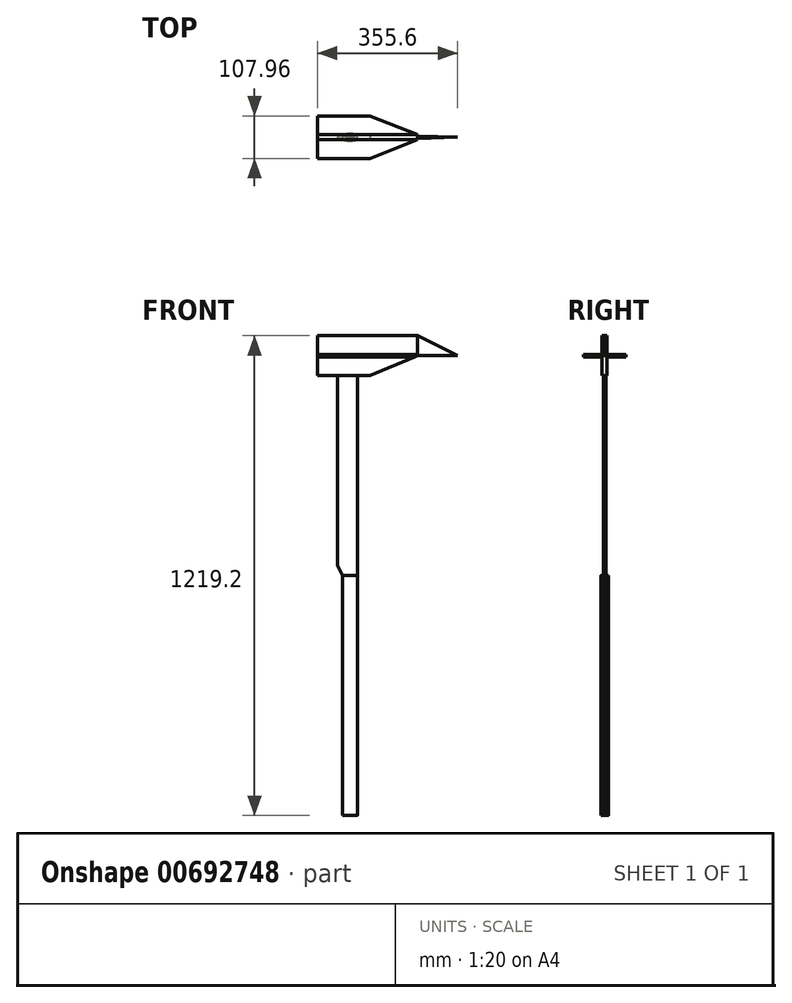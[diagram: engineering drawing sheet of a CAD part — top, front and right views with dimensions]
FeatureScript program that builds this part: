
annotation { "Feature Type Name" : "Feature", "Feature Type Description" : "" }
export const myFeature = defineFeature(function(context is Context, id is Id, definition is map)
    precondition{}
    {
        {
            var Q0;
            Q0=qCreatedBy(makeId("Top.planeOp"),FACE);
            var sketch = newSketch(context, id + "F0", { "sketchPlane" : qUnion([Q0])});
            skLineSegment(sketch, "E0.bottom", {"start": v(25.4, -3.17) * mm, "end": v(-25.4, -3.18) * mm});
            skLineSegment(sketch, "E0.top", {"start": v(25.4, 3.18) * mm, "end": v(-25.4, 3.18) * mm});
            skLineSegment(sketch, "E0.left", {"start": v(25.4, -3.17) * mm, "end": v(25.4, 3.18) * mm});
            skLineSegment(sketch, "E0.right", {"start": v(-25.4, -3.18) * mm, "end": v(-25.4, 3.18) * mm});
            skPoint(sketch, "E0.middle", {"position": v(0, 0) * mm});
            skSolve(sketch);
        }
        {
            var Q0;
            Q0 = qSketchRegion(id + "F0", true);
            extrude(context, id + "F1", {"entities" : qUnion([Q0]), "depth" : 1219.2 * mm, "offsetDistance" : 25.4 * mm});
        }
        {
            var Q0;
            Q0=qCreatedBy(makeId("Top.planeOp"),FACE);
            var sketch = newSketch(context, id + "F2", { "sketchPlane" : qUnion([Q0])});
            skLineSegment(sketch, "E1.bottom", {"start": v(-76.2, 53.98) * mm, "end": v(279.4, 53.98) * mm});
            skLineSegment(sketch, "E1.top", {"start": v(-76.2, -53.98) * mm, "end": v(279.4, -53.98) * mm});
            skLineSegment(sketch, "E1.left", {"start": v(-76.2, 53.98) * mm, "end": v(-76.2, -53.98) * mm});
            skLineSegment(sketch, "E1.right", {"start": v(279.4, 53.98) * mm, "end": v(279.4, -53.98) * mm, "construction": true});
            skPoint(sketch, "E2", {"position": v(279.4, 0) * mm});
            skPoint(sketch, "E3", {"position": v(177.8, 3.18) * mm});
            skPoint(sketch, "E4", {"position": v(177.8, -3.18) * mm});
            skPoint(sketch, "E5", {"position": v(177.8, 6.35) * mm});
            skPoint(sketch, "E6", {"position": v(177.8, -6.35) * mm});
            skPoint(sketch, "E7", {"position": v(57.15, 53.98) * mm});
            skPoint(sketch, "E8", {"position": v(57.16, -53.98) * mm});
            skLineSegment(sketch, "E9", {"start": v(57.15, 53.97) * mm, "end": v(177.8, 6.35) * mm});
            skLineSegment(sketch, "E10", {"start": v(177.8, 6.35) * mm, "end": v(177.8, 3.18) * mm});
            skLineSegment(sketch, "E11", {"start": v(177.8, 3.18) * mm, "end": v(279.4, 0) * mm});
            skLineSegment(sketch, "E12", {"start": v(177.8, -3.18) * mm, "end": v(177.8, -6.35) * mm});
            skLineSegment(sketch, "E13", {"start": v(177.8, -3.18) * mm, "end": v(279.4, 0) * mm});
            skLineSegment(sketch, "E14", {"start": v(177.8, -6.35) * mm, "end": v(57.16, -53.98) * mm});
            skSolve(sketch);
        }
        {
            var Q0;
            Q0 = qSketchRegion(id + "F2", true);
            extrude(context, id + "F3", {"entities" : qUnion([Q0]), "operationType" : NewBodyOperationType.ADD, "depth" : 1219.2 * mm, "offsetDistance" : 25.4 * mm, "hasSecondDirection" : true, "secondDirectionOppositeDirection" : false, "secondDirectionDepth" : 1117.6 * mm});
        }
        {
            var Q0;
            Q0=qCreatedBy(makeId("Front.planeOp"),FACE);
            var sketch = newSketch(context, id + "F4", { "sketchPlane" : qUnion([Q0])});
            skLineSegment(sketch, "E15.bottom", {"start": v(-76.2, 1117.6) * mm, "end": v(177.8, 1117.6) * mm, "construction": true});
            skLineSegment(sketch, "E15.top", {"start": v(-76.2, 1219.2) * mm, "end": v(177.8, 1219.2) * mm, "construction": true});
            skLineSegment(sketch, "E15.left", {"start": v(-76.2, 1117.6) * mm, "end": v(-76.2, 1219.2) * mm, "construction": true});
            skLineSegment(sketch, "E15.right", {"start": v(177.8, 1117.6) * mm, "end": v(177.8, 1219.2) * mm, "construction": true});
            skLineSegment(sketch, "E16.bottom", {"start": v(177.8, 1219.2) * mm, "end": v(279.4, 1219.2) * mm, "construction": true});
            skLineSegment(sketch, "E16.top", {"start": v(177.8, 1168.4) * mm, "end": v(279.4, 1168.4) * mm, "construction": true});
            skLineSegment(sketch, "E16.left", {"start": v(177.8, 1219.2) * mm, "end": v(177.8, 1168.4) * mm, "construction": true});
            skLineSegment(sketch, "E16.right", {"start": v(279.4, 1219.2) * mm, "end": v(279.4, 1168.4) * mm, "construction": true});
            skLineSegment(sketch, "E17", {"start": v(279.4, 1168.4) * mm, "end": v(177.8, 1219.2) * mm});
            skLineSegment(sketch, "E18", {"start": v(279.4, 1168.4) * mm, "end": v(177.8, 1168.4) * mm});
            skLineSegment(sketch, "E19", {"start": v(177.8, 1168.4) * mm, "end": v(57.15, 1117.6) * mm});
            skLineSegment(sketch, "E20", {"start": v(57.15, 1117.6) * mm, "end": v(279.4, 1117.6) * mm});
            skLineSegment(sketch, "E21", {"start": v(279.4, 1117.6) * mm, "end": v(279.4, 1168.4) * mm});
            skLineSegment(sketch, "E22", {"start": v(279.4, 1168.4) * mm, "end": v(279.4, 1219.2) * mm});
            skLineSegment(sketch, "E23", {"start": v(279.4, 1219.2) * mm, "end": v(177.8, 1219.2) * mm});
            skPoint(sketch, "E24", {"position": v(25.4, 1117.6) * mm});
            skSolve(sketch);
        }
        {
            var Q0;
            Q0 = qSketchRegion(id + "F4", true);
            extrude(context, id + "F5", {"entities" : qUnion([Q0]), "operationType" : NewBodyOperationType.REMOVE, "oppositeDirection" : true, "depth" : 76.2 * mm, "offsetDistance" : 25.4 * mm, "hasSecondDirection" : true, "secondDirectionOppositeDirection" : false, "secondDirectionDepth" : 76.2 * mm});
        }
        {
            var Q0;
            Q0=qCreatedBy(makeId("Right.planeOp"),FACE);
            var sketch = newSketch(context, id + "F6", { "sketchPlane" : qUnion([Q0])});
            skLineSegment(sketch, "E25.bottom", {"start": v(53.97, 1219.2) * mm, "end": v(-53.98, 1219.2) * mm, "construction": true});
            skLineSegment(sketch, "E25.top", {"start": v(53.98, 1117.6) * mm, "end": v(-53.97, 1117.6) * mm, "construction": true});
            skLineSegment(sketch, "E25.left", {"start": v(53.97, 1219.2) * mm, "end": v(53.98, 1117.6) * mm, "construction": true});
            skLineSegment(sketch, "E25.right", {"start": v(-53.98, 1219.2) * mm, "end": v(-53.97, 1117.6) * mm, "construction": true});
            skLineSegment(sketch, "E26.bottom", {"start": v(-53.98, 1219.2) * mm, "end": v(-6.35, 1219.2) * mm});
            skLineSegment(sketch, "E26.top", {"start": v(-53.98, 1171.58) * mm, "end": v(-6.35, 1171.58) * mm});
            skLineSegment(sketch, "E26.left", {"start": v(-53.98, 1219.2) * mm, "end": v(-53.98, 1171.58) * mm});
            skLineSegment(sketch, "E26.right", {"start": v(-6.35, 1219.2) * mm, "end": v(-6.35, 1171.58) * mm});
            skLineSegment(sketch, "E27.bottom", {"start": v(-53.97, 1117.6) * mm, "end": v(-6.35, 1117.6) * mm});
            skLineSegment(sketch, "E27.top", {"start": v(-53.98, 1165.23) * mm, "end": v(-6.35, 1165.23) * mm});
            skLineSegment(sketch, "E27.left", {"start": v(-53.97, 1117.6) * mm, "end": v(-53.97, 1165.23) * mm});
            skLineSegment(sketch, "E27.right", {"start": v(-6.35, 1117.6) * mm, "end": v(-6.35, 1165.23) * mm});
            skLineSegment(sketch, "E28.bottom", {"start": v(53.98, 1117.6) * mm, "end": v(6.35, 1117.6) * mm});
            skLineSegment(sketch, "E28.top", {"start": v(53.98, 1165.23) * mm, "end": v(6.35, 1165.23) * mm});
            skLineSegment(sketch, "E28.left", {"start": v(53.98, 1117.6) * mm, "end": v(53.98, 1165.23) * mm});
            skLineSegment(sketch, "E28.right", {"start": v(6.35, 1117.6) * mm, "end": v(6.35, 1165.23) * mm});
            skLineSegment(sketch, "E29.bottom", {"start": v(53.97, 1219.2) * mm, "end": v(6.35, 1219.2) * mm});
            skLineSegment(sketch, "E29.top", {"start": v(53.98, 1171.58) * mm, "end": v(6.35, 1171.58) * mm});
            skLineSegment(sketch, "E29.left", {"start": v(53.97, 1219.2) * mm, "end": v(53.97, 1171.58) * mm});
            skLineSegment(sketch, "E29.right", {"start": v(6.35, 1219.2) * mm, "end": v(6.35, 1171.58) * mm});
            skSolve(sketch);
        }
        {
            var Q0;
            Q0 = qSketchRegion(id + "F6", true);
            extrude(context, id + "F7", {"entities" : qUnion([Q0]), "operationType" : NewBodyOperationType.REMOVE, "oppositeDirection" : true, "depth" : 101.6 * mm, "offsetDistance" : 25.4 * mm, "hasSecondDirection" : true, "secondDirectionOppositeDirection" : false, "secondDirectionDepth" : 254 * mm});
        }
        {
            var Q0;
            Q0=qCreatedBy(makeId("Top.planeOp"),FACE);
            var sketch = newSketch(context, id + "F8", { "sketchPlane" : qUnion([Q0])});
            skLineSegment(sketch, "E30", {"start": v(-12.7, 3.18) * mm, "end": v(25.4, 3.18) * mm});
            skLineSegment(sketch, "E31", {"start": v(25.4, -3.18) * mm, "end": v(-12.7, -3.18) * mm});
            skArc(sketch, "E32", {"start": v(25.4, 3.17) * mm, "mid": v(6.35, 3.03) * mm, "end": v(-12.7, 3.17) * mm});
            skArc(sketch, "E33", {"start": v(25.4, 6.35) * mm, "mid": v(6.35, 9.53) * mm, "end": v(-12.7, 6.35) * mm});
            skArc(sketch, "E34", {"start": v(-12.7, -6.35) * mm, "mid": v(6.35, -9.52) * mm, "end": v(25.4, -6.35) * mm});
            skPoint(sketch, "E35", {"position": v(-9.53, 7.34) * mm});
            skArc(sketch, "E36", {"start": v(-9.52, 7.34) * mm, "mid": v(-11.8, 5.79) * mm, "end": v(-12.7, 3.18) * mm});
            skPoint(sketch, "E37", {"position": v(-9.53, -7.34) * mm});
            skPoint(sketch, "E38", {"position": v(22.23, 7.34) * mm});
            skPoint(sketch, "E39", {"position": v(22.23, -7.34) * mm});
            skArc(sketch, "E40", {"start": v(-12.7, -3.18) * mm, "mid": v(-11.8, -5.79) * mm, "end": v(-9.53, -7.34) * mm});
            skArc(sketch, "E41", {"start": v(22.23, -7.34) * mm, "mid": v(24.5, -5.79) * mm, "end": v(25.4, -3.18) * mm});
            skArc(sketch, "E42", {"start": v(25.4, 3.18) * mm, "mid": v(24.5, 5.79) * mm, "end": v(22.22, 7.34) * mm});
            skSolve(sketch);
        }
        {
            var Q0;
            Q0 = qSketchRegion(id + "F8", true);
            extrude(context, id + "F9", {"entities" : qUnion([Q0]), "depth" : 609.6 * mm, "offsetDistance" : 25.4 * mm});
        }
        {
            var Q0;
            Q0=qCreatedBy(makeId("Front.planeOp"),FACE);
            var sketch = newSketch(context, id + "F10", { "sketchPlane" : qUnion([Q0])});
            skLineSegment(sketch, "E43", {"start": v(-12.7, 609.6) * mm, "end": v(-25.4, 635) * mm});
            skPoint(sketch, "E44", {"position": v(0, 609.6) * mm});
            skLineSegment(sketch, "E45", {"start": v(0, 609.6) * mm, "end": v(-25.47, 609.6) * mm, "construction": true});
            skLineSegment(sketch, "E46", {"start": v(-12.7, 609.6) * mm, "end": v(-12.7, 650.3) * mm, "construction": true});
            skLineSegment(sketch, "E47", {"start": v(-25.4, 635) * mm, "end": v(-25.4, 0) * mm});
            skLineSegment(sketch, "E48", {"start": v(-25.4, 0) * mm, "end": v(-12.7, 0) * mm});
            skLineSegment(sketch, "E49", {"start": v(-12.7, 0) * mm, "end": v(-12.7, 609.6) * mm});
            skSolve(sketch);
        }
        {
            var Q0;
            Q0 = qSketchRegion(id + "F10", true);
            extrude(context, id + "F11", {"entities" : qUnion([Q0]), "operationType" : NewBodyOperationType.REMOVE, "oppositeDirection" : true, "depth" : 25.4 * mm, "offsetDistance" : 25.4 * mm, "hasSecondDirection" : true, "secondDirectionOppositeDirection" : false, "secondDirectionDepth" : 25.4 * mm});
        }
    });
